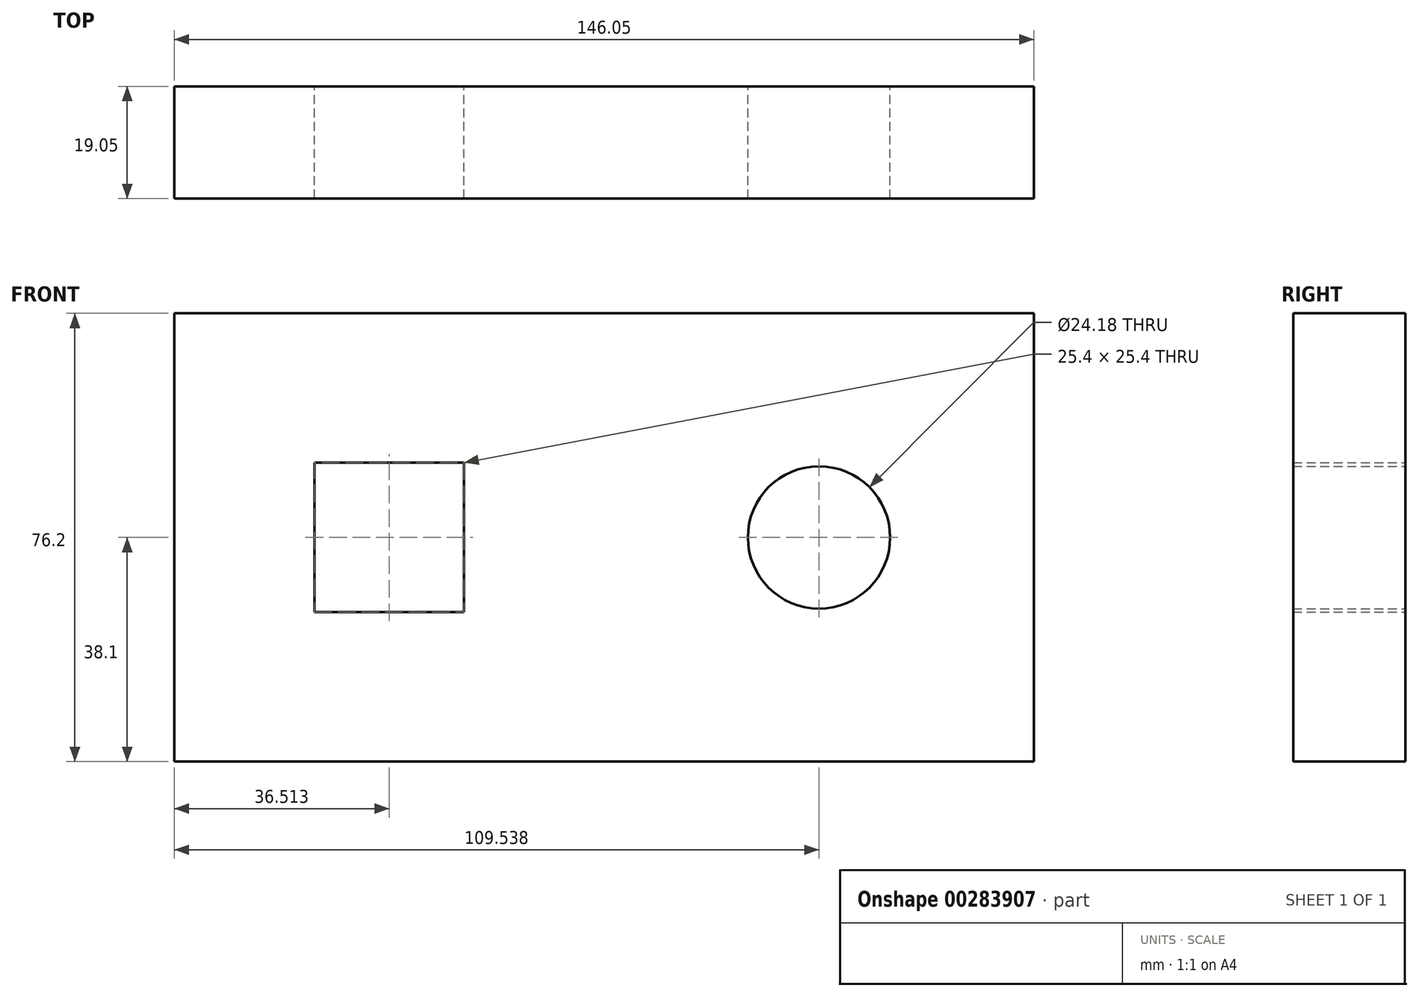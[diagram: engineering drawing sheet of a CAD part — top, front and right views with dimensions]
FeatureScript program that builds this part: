
annotation { "Feature Type Name" : "Feature", "Feature Type Description" : "" }
export const myFeature = defineFeature(function(context is Context, id is Id, definition is map)
    precondition{}
    {
        {
            var Q0;
            Q0=qCreatedBy(makeId("Front.planeOp"),FACE);
            var sketch = newSketch(context, id + "F0", { "sketchPlane" : qUnion([Q0])});
            skLineSegment(sketch, "E0.bottom", {"start": v(0, 0) * mm, "end": v(-146.05, 0) * mm});
            skLineSegment(sketch, "E0.top", {"start": v(0, 76.2) * mm, "end": v(-146.05, 76.2) * mm});
            skLineSegment(sketch, "E0.left", {"start": v(0, 0) * mm, "end": v(0, 76.2) * mm});
            skLineSegment(sketch, "E0.right", {"start": v(-146.05, 0) * mm, "end": v(-146.05, 76.2) * mm});
            skLineSegment(sketch, "E1.bottom", {"start": v(-122.24, 50.8) * mm, "end": v(-96.84, 50.8) * mm});
            skLineSegment(sketch, "E1.top", {"start": v(-122.24, 25.4) * mm, "end": v(-96.84, 25.4) * mm});
            skLineSegment(sketch, "E1.left", {"start": v(-122.24, 50.8) * mm, "end": v(-122.24, 25.4) * mm});
            skLineSegment(sketch, "E1.right", {"start": v(-96.84, 50.8) * mm, "end": v(-96.84, 25.4) * mm});
            skCircle(sketch, "E2", {"center": v(-36.51, 38.1) * mm, "radius": 12.1 * mm});
            skSolve(sketch);
        }
        {
            var Q0;
            Q0 = qSketchRegion(id + "F0", true);
            extrude(context, id + "F1", {"entities" : qUnion([Q0]), "depth" : 19.05 * mm});
        }
    });
